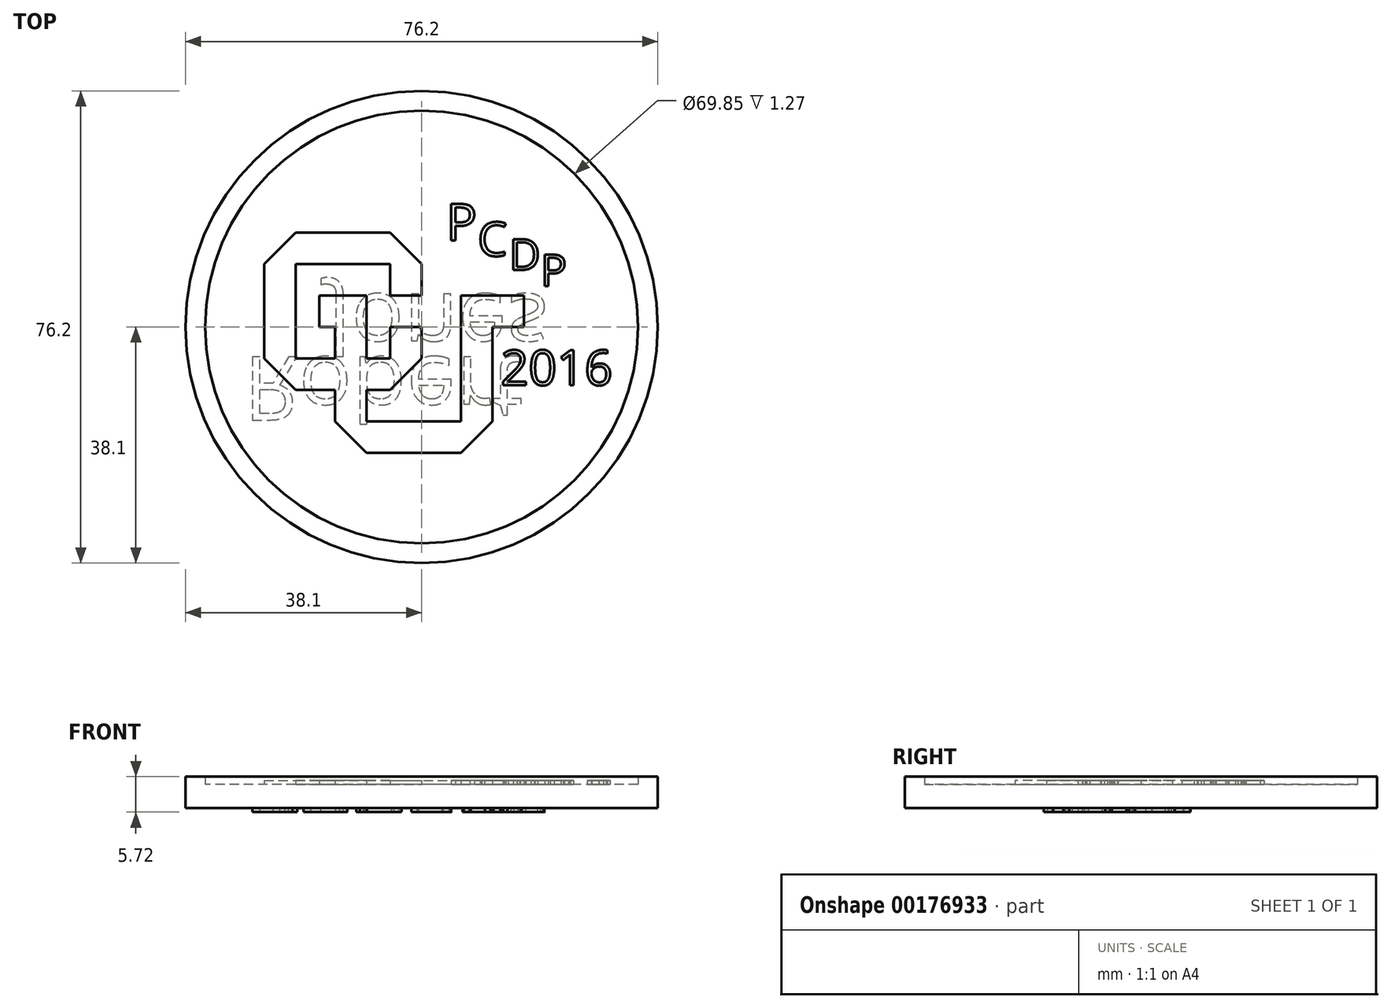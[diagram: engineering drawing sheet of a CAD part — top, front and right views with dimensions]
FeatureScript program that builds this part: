
annotation { "Feature Type Name" : "Feature", "Feature Type Description" : "" }
export const myFeature = defineFeature(function(context is Context, id is Id, definition is map)
    precondition{}
    {
        {
            var Q0;
            Q0=qCreatedBy(makeId("Top.planeOp"),FACE);
            var sketch = newSketch(context, id + "F0", { "sketchPlane" : qUnion([Q0])});
            skCircle(sketch, "E0", {"center": v(0, 0) * mm, "radius": 38.1 * mm});
            skSolve(sketch);
        }
        {
            var Q0;
            Q0=makeQuery(id+"F0.imprint","IMPRINT",FACE,{"disambiguationData":[TD([[makeQuery(id+"F0.imprint","IMPRINT",EDGE,{"derivedFrom":sQuery(id+"F0.wireOp",EDGE,"E0")}),1.0]])]});
            extrude(context, id + "F1", {"entities" : qUnion([Q0]), "depth" : 3.8 * mm});
        }
        {
            var Q0;
            Q0=makeQuery(id+"F1.opExtrude","CAP_FACE",FACE,{"disambiguationData":[OSD([sQuery(id+"F0.wireOp",EDGE,"E0")])],"isStart":false});
            var sketch = newSketch(context, id + "F2", { "sketchPlane" : qUnion([Q0])});
            skLineSegment(sketch, "E1", {"start": v(0, 0) * mm, "end": v(0, -5.08) * mm});
            skLineSegment(sketch, "E2", {"start": v(0, -5.08) * mm, "end": v(-5.08, -10.16) * mm});
            skLineSegment(sketch, "E3", {"start": v(-5.08, -10.16) * mm, "end": v(-8.89, -10.16) * mm});
            skLineSegment(sketch, "E4", {"start": v(-20.32, -10.16) * mm, "end": v(-25.4, -5.08) * mm});
            skLineSegment(sketch, "E5", {"start": v(-25.4, -5.08) * mm, "end": v(-25.4, 10.16) * mm});
            skLineSegment(sketch, "E6", {"start": v(-25.4, 10.16) * mm, "end": v(-20.32, 15.24) * mm});
            skLineSegment(sketch, "E7", {"start": v(-20.32, 15.24) * mm, "end": v(-5.08, 15.24) * mm});
            skLineSegment(sketch, "E8", {"start": v(-5.08, 15.24) * mm, "end": v(0, 10.16) * mm});
            skLineSegment(sketch, "E9", {"start": v(-5.08, 10.16) * mm, "end": v(-20.32, 10.16) * mm});
            skLineSegment(sketch, "E10", {"start": v(-20.32, 10.16) * mm, "end": v(-20.32, -5.08) * mm});
            skLineSegment(sketch, "E11", {"start": v(-20.32, -5.08) * mm, "end": v(-13.97, -5.08) * mm});
            skLineSegment(sketch, "E12", {"start": v(-5.08, -5.08) * mm, "end": v(-5.08, 0) * mm});
            skLineSegment(sketch, "E13", {"start": v(-5.08, 0) * mm, "end": v(0, 0) * mm});
            skPoint(sketch, "E14.end.orphan", {"position": v(-5.08, 13.57) * mm});
            skLineSegment(sketch, "E15", {"start": v(-5.08, 10.16) * mm, "end": v(-5.08, 5.08) * mm});
            skLineSegment(sketch, "E16", {"start": v(-5.08, 5.08) * mm, "end": v(0, 5.08) * mm});
            skLineSegment(sketch, "E17", {"start": v(0, 5.08) * mm, "end": v(0, 10.16) * mm});
            skLineSegment(sketch, "E18", {"start": v(-16.5, 5.08) * mm, "end": v(-16.5, 0) * mm});
            skLineSegment(sketch, "E19", {"start": v(-16.5, 0) * mm, "end": v(-13.97, 0) * mm});
            skLineSegment(sketch, "E20", {"start": v(-13.97, 0) * mm, "end": v(-13.97, -5.08) * mm});
            skLineSegment(sketch, "E21", {"start": v(-13.97, -15.24) * mm, "end": v(-8.89, -20.32) * mm});
            skLineSegment(sketch, "E22", {"start": v(-8.89, -20.32) * mm, "end": v(6.35, -20.32) * mm});
            skLineSegment(sketch, "E23", {"start": v(6.35, -20.32) * mm, "end": v(11.43, -15.24) * mm});
            skLineSegment(sketch, "E24", {"start": v(11.43, -15.24) * mm, "end": v(11.43, 0) * mm});
            skLineSegment(sketch, "E25", {"start": v(11.43, 0) * mm, "end": v(16.51, 0) * mm});
            skLineSegment(sketch, "E26", {"start": v(16.51, 5.08) * mm, "end": v(6.35, 5.08) * mm});
            skLineSegment(sketch, "E27", {"start": v(6.35, -15.24) * mm, "end": v(-8.89, -15.24) * mm});
            skLineSegment(sketch, "E28", {"start": v(-8.89, -15.24) * mm, "end": v(-8.89, -10.16) * mm});
            skLineSegment(sketch, "E29", {"start": v(-8.89, 5.08) * mm, "end": v(-16.5, 5.08) * mm});
            skLineSegment(sketch, "E30", {"start": v(16.51, 0) * mm, "end": v(16.51, 5.08) * mm});
            skLineSegment(sketch, "E31", {"start": v(6.35, 5.08) * mm, "end": v(6.35, -15.24) * mm});
            skCircle(sketch, "E32", {"center": v(0, 0) * mm, "radius": 38.1 * mm});
            skCircle(sketch, "E33.0", {"center": v(0, 0) * mm, "radius": 34.93 * mm});
            skLineSegment(sketch, "E34.trimOffspring", {"start": v(-8.89, -5.08) * mm, "end": v(-5.08, -5.08) * mm});
            skLineSegment(sketch, "E35.trimOffspring", {"start": v(-13.97, -10.16) * mm, "end": v(-13.97, -15.24) * mm});
            skLineSegment(sketch, "E36.trimOffspring", {"start": v(-8.89, -5.08) * mm, "end": v(-8.89, 5.08) * mm});
            skLineSegment(sketch, "E37.trimOffspring", {"start": v(-13.97, -10.16) * mm, "end": v(-20.32, -10.16) * mm});
            skSolve(sketch);
        }
        {
            var Q0;
            Q0=makeQuery(id+"F2.imprint","IMPRINT",FACE,{"disambiguationData":[TD([[makeQuery(id+"F2.imprint","IMPRINT",EDGE,{"derivedFrom":sQuery(id+"F2.wireOp",EDGE,"E32")}),1.0]])]});
            var Q1;
            Q1=makeQuery(id+"F2.imprint","IMPRINT",FACE,{"disambiguationData":[TD([[makeQuery(id+"F2.imprint","IMPRINT",EDGE,{"derivedFrom":sQuery(id+"F2.wireOp",EDGE,"E1")}),-1.0]])]});
            extrude(context, id + "F3", {"entities" : qUnion([Q0, Q1]), "operationType" : NewBodyOperationType.ADD, "depth" : 0.64 * mm});
        }
        {
            var Q0;
            Q0=makeQuery(id+"F1.opExtrude","CAP_FACE",FACE,{"disambiguationData":[OSD([sQuery(id+"F0.wireOp",EDGE,"E0")])],"isStart":true});
            var sketch = newSketch(context, id + "F4", { "sketchPlane" : qUnion([Q0])});
            skText(sketch, "E38", { "text": "Robert\n", "fontName": "OpenSans-Regular.ttf"});
            skText(sketch, "E39", { "text": "Jones", "fontName": "OpenSans-Regular.ttf"});
            skCircle(sketch, "E40", {"center": v(0, 0) * mm, "radius": 38.1 * mm});
            skCircle(sketch, "E41.0", {"center": v(0, 0) * mm, "radius": 34.93 * mm});
            const initialGuessF4  = {"E38": [-0.0254, 0.00127, 1, 0, 0.01143], "E39": [-0.01493, -0.0127, 1, 0, 0.01397]};
            skSetInitialGuess(sketch, initialGuessF4);
            skSolve(sketch);
        }
        {
            var Q0;
            Q0=makeQuery(id+"F1.opExtrude","CAP_FACE",FACE,{"disambiguationData":[OSD([sQuery(id+"F0.wireOp",EDGE,"E0")])],"isStart":false});
            var sketch = newSketch(context, id + "F5", { "sketchPlane" : qUnion([Q0])});
            skText(sketch, "E42", { "text": "P", "fontName": "OpenSans-Regular.ttf"});
            skText(sketch, "E43", { "text": "C\n", "fontName": "OpenSans-Regular.ttf"});
            skText(sketch, "E44", { "text": "D", "fontName": "OpenSans-Regular.ttf"});
            skText(sketch, "E45", { "text": "P", "fontName": "OpenSans-Regular.ttf"});
            const initialGuessF5  = {"E42": [0.00394, 0.01398, 1, 0, 0.00594], "E43": [0.00902, 0.01146, 1, 0, 0.0055], "E44": [0.0141, 0.00921, 1, 0, 0.005], "E45": [0.01918, 0.00663, 1, 0, 0.00508]};
            skSetInitialGuess(sketch, initialGuessF5);
            skSolve(sketch);
        }
        {
            var Q0;
            Q0 = qSketchRegion(id + "F5", true);
            var Q1;
            Q1=makeQuery(id+"F3.opExtrude","CAP_FACE",FACE,{"disambiguationData":[OSD([sQuery(id+"F2.wireOp",EDGE,"E32"),sQuery(id+"F2.wireOp",EDGE,"E33.0")])],"isStart":false});
            extrude(context, id + "F6", {"entities" : qUnion([Q0, Q1]), "operationType" : NewBodyOperationType.ADD, "depth" : 0.64 * mm});
        }
        {
            var Q0;
            Q0=sQuery(id+"F4.wireOp",EDGE,"E41.0");
            var Q1;
            Q1=sQuery(id+"F4.wireOp",EDGE,"E40");
            extrude(context, id + "F7", {"bodyType" : ToolBodyType.SURFACE, "surfaceEntities" : qUnion([Q0, Q1]), "depth" : 0.64 * mm});
        }
        {
            var Q0;
            Q0=makeQuery(id+"F1.opExtrude","CAP_FACE",FACE,{"disambiguationData":[OSD([sQuery(id+"F0.wireOp",EDGE,"E0")])],"isStart":true});
            var sketch = newSketch(context, id + "F8", { "sketchPlane" : qUnion([Q0])});
            skText(sketch, "E46", { "text": "Robert ", "fontName": "OpenSans-Regular.ttf"});
            skText(sketch, "E47", { "text": "Jones", "fontName": "OpenSans-Regular.ttf"});
            const initialGuessF8  = {"E46": [-0.02868, 0.00483, 1, 0, 0.01028], "E47": [-0.01513, -0.00533, 1, 0, 0.01016]};
            skSetInitialGuess(sketch, initialGuessF8);
            skSolve(sketch);
        }
        {
            var Q0;
            Q0 = qSketchRegion(id + "F8", true);
            extrude(context, id + "F9", {"entities" : qUnion([Q0]), "operationType" : NewBodyOperationType.ADD, "depth" : 0.64 * mm});
        }
        {
            var Q0;
            Q0=makeQuery(id+"F6.boolean.opBoolean","SPLIT",FACE,{"disambiguationData":[TD([makeQuery(id+"F3.opExtrude","SWEPT_FACE",FACE,{"disambiguationData":[OSD([sQuery(id+"F2.wireOp",EDGE,"E1")])]})])],"derivedFrom":makeQuery(id+"F1.opExtrude","CAP_FACE",FACE,{"disambiguationData":[OSD([sQuery(id+"F0.wireOp",EDGE,"E0")])],"isStart":false})});
            var sketch = newSketch(context, id + "F10", { "sketchPlane" : qUnion([Q0])});
            skText(sketch, "E48", { "text": "2016", "fontName": "OpenSans-Regular.ttf"});
            const initialGuessF10  = {"E48": [0.01276, -0.0094, 1, 0, 0.00568]};
            skSetInitialGuess(sketch, initialGuessF10);
            skSolve(sketch);
        }
        {
            var Q0;
            Q0 = qSketchRegion(id + "F10", true);
            extrude(context, id + "F11", {"entities" : qUnion([Q0]), "operationType" : NewBodyOperationType.ADD, "depth" : 0.64 * mm});
        }
    });
